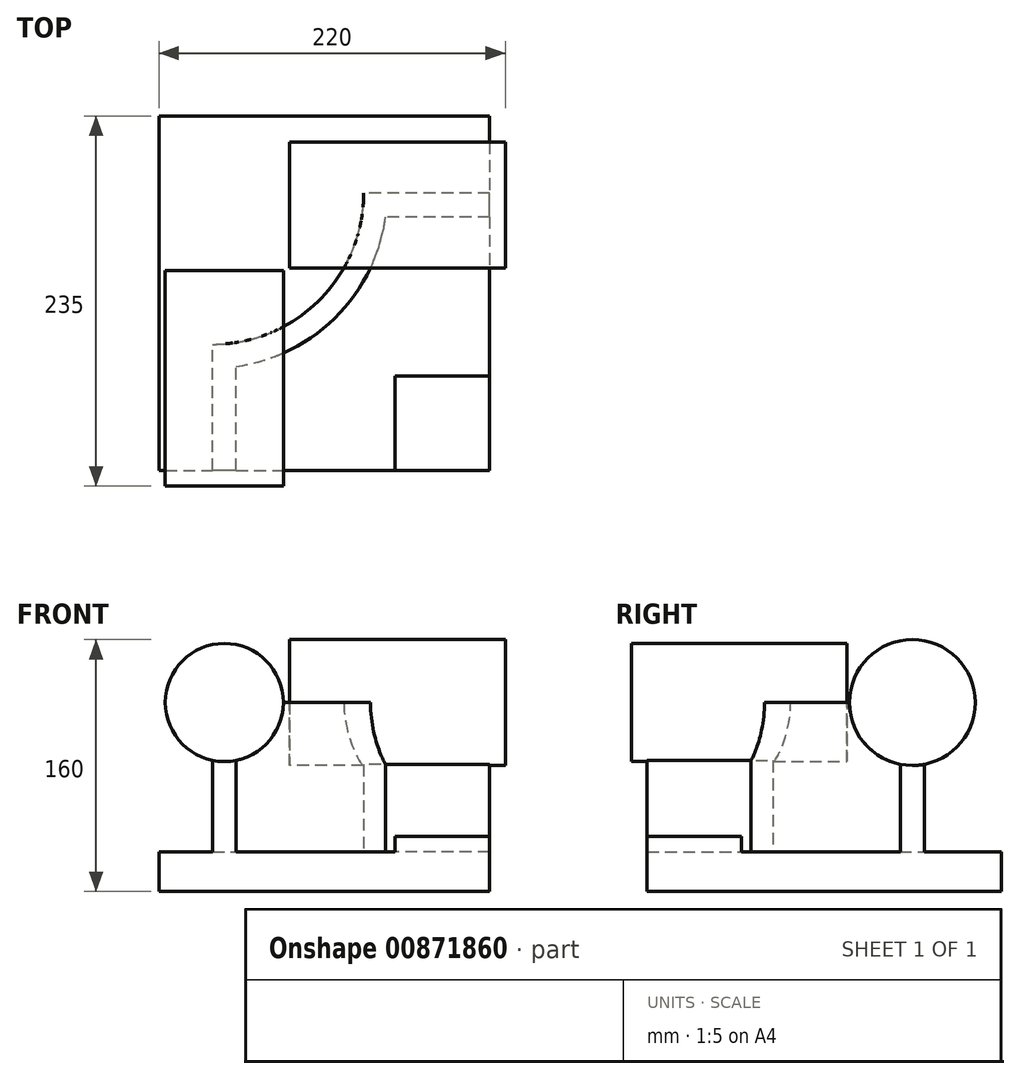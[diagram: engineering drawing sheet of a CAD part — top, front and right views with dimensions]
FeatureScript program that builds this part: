
annotation { "Feature Type Name" : "Feature", "Feature Type Description" : "" }
export const myFeature = defineFeature(function(context is Context, id is Id, definition is map)
    precondition{}
    {
        {
            var Q0;
            Q0=qCreatedBy(makeId("Top.planeOp"),FACE);
            var sketch = newSketch(context, id + "F0", { "sketchPlane" : qUnion([Q0])});
            skLineSegment(sketch, "E0.bottom", {"start": v(-105, 112.5) * mm, "end": v(105, 112.5) * mm});
            skLineSegment(sketch, "E0.top", {"start": v(-105, -112.5) * mm, "end": v(105, -112.5) * mm});
            skLineSegment(sketch, "E0.left", {"start": v(-105, 112.5) * mm, "end": v(-105, -112.5) * mm});
            skLineSegment(sketch, "E0.right", {"start": v(105, 112.5) * mm, "end": v(105, -112.5) * mm});
            skPoint(sketch, "E0.middle", {"position": v(0, 0) * mm});
            skSolve(sketch);
        }
        {
            var Q0;
            Q0=makeQuery(id+"F0.imprint","IMPRINT",FACE,{"disambiguationData":[TD([[makeQuery(id+"F0.imprint","IMPRINT",EDGE,{"derivedFrom":sQuery(id+"F0.wireOp",EDGE,"E0.bottom")}),-1.0]])]});
            extrude(context, id + "F1", {"entities" : qUnion([Q0]), "depth" : 25 * mm, "offsetDistance" : 25 * mm});
        }
        {
            var Q0;
            Q0=makeQuery(id+"F1.opExtrude","CAP_FACE",FACE,{"disambiguationData":[OSD([sQuery(id+"F0.wireOp",EDGE,"E0.bottom"),sQuery(id+"F0.wireOp",EDGE,"E0.top"),sQuery(id+"F0.wireOp",EDGE,"E0.left"),sQuery(id+"F0.wireOp",EDGE,"E0.right")])],"isStart":false});
            var sketch = newSketch(context, id + "F2", { "sketchPlane" : qUnion([Q0])});
            skLineSegment(sketch, "E1", {"start": v(-71, -112.5) * mm, "end": v(-71, -32.5) * mm});
            skLineSegment(sketch, "E2", {"start": v(105, 63.5) * mm, "end": v(25, 63.5) * mm});
            skArc(sketch, "E3", {"start": v(-71, -32.5) * mm, "mid": v(-3.12, -4.38) * mm, "end": v(25, 63.5) * mm});
            skLineSegment(sketch, "E4", {"start": v(-71, 63.5) * mm, "end": v(25, 63.5) * mm, "construction": true});
            skLineSegment(sketch, "E5", {"start": v(-71, 63.5) * mm, "end": v(-71, -32.5) * mm, "construction": true});
            skLineSegment(sketch, "E6.0", {"start": v(-56, -112.5) * mm, "end": v(-56, -46.48) * mm});
            skArc(sketch, "E6.1", {"start": v(-56, -46.48) * mm, "mid": v(7.49, -14.99) * mm, "end": v(38.98, 48.5) * mm});
            skLineSegment(sketch, "E6.2", {"start": v(105, 48.5) * mm, "end": v(38.98, 48.5) * mm});
            skLineSegment(sketch, "E7.0.0", {"start": v(-105, 112.5) * mm, "end": v(-105, -112.5) * mm});
            skLineSegment(sketch, "E7.0.1", {"start": v(-105, -112.5) * mm, "end": v(105, -112.5) * mm});
            skLineSegment(sketch, "E7.0.2", {"start": v(105, -112.5) * mm, "end": v(105, 112.5) * mm});
            skLineSegment(sketch, "E7.0.3", {"start": v(105, 112.5) * mm, "end": v(-105, 112.5) * mm});
            skSolve(sketch);
        }
        {
            var Q0;
            {var subQ2=sQuery(id+"F2.wireOp",EDGE,"E1");Q0=makeQuery(id+"F2.imprint","IMPRINT",FACE,{"disambiguationData":[TD([[makeQuery(id+"F2.imprint","IMPRINT",EDGE,{"derivedFrom":subQ2}),-1.0]])]});}
            extrude(context, id + "F3", {"entities" : qUnion([Q0]), "operationType" : NewBodyOperationType.ADD, "depth" : 95 * mm, "offsetDistance" : 25 * mm});
        }
        {
            var Q0;
            Q0=makeQuery(id+"F3.boolean.opBoolean","MERGE",FACE,{"derivedFrom":[makeQuery(id+"F1.opExtrude","SWEPT_FACE",FACE,{"disambiguationData":[OSD([sQuery(id+"F0.wireOp",EDGE,"E0.top")])]}),makeQuery(id+"F3.opExtrude","SWEPT_FACE",FACE,{"disambiguationData":[OSD([sQuery(id+"F2.wireOp",EDGE,"E7.0.1")])]})]});
            var sketch = newSketch(context, id + "F4", { "sketchPlane" : qUnion([Q0])});
            skCircle(sketch, "E8", {"center": v(-63.5, 120) * mm, "radius": 37.5 * mm});
            skSolve(sketch);
        }
        {
            var Q0;
            Q0 = qSketchRegion(id + "F4", true);
            extrude(context, id + "F5", {"entities" : qUnion([Q0]), "operationType" : NewBodyOperationType.ADD, "depth" : 10 * mm, "offsetDistance" : 25 * mm, "hasSecondDirection" : true, "secondDirectionOppositeDirection" : true, "secondDirectionDepth" : (137 - 10) * mm});
        }
        {
            var Q0;
            Q0=makeQuery(id+"F3.boolean.opBoolean","MERGE",FACE,{"derivedFrom":[makeQuery(id+"F1.opExtrude","SWEPT_FACE",FACE,{"disambiguationData":[OSD([sQuery(id+"F0.wireOp",EDGE,"E0.right")])]}),makeQuery(id+"F3.opExtrude","SWEPT_FACE",FACE,{"disambiguationData":[OSD([sQuery(id+"F2.wireOp",EDGE,"E7.0.2")])]})]});
            var sketch = newSketch(context, id + "F6", { "sketchPlane" : qUnion([Q0])});
            skCircle(sketch, "E9", {"center": v(56, 120) * mm, "radius": 40 * mm});
            skSolve(sketch);
        }
        {
            var Q0;
            Q0 = qSketchRegion(id + "F6", true);
            extrude(context, id + "F7", {"entities" : qUnion([Q0]), "operationType" : NewBodyOperationType.ADD, "depth" : 10 * mm, "offsetDistance" : 25 * mm, "hasSecondDirection" : true, "secondDirectionOppositeDirection" : true, "secondDirectionDepth" : (137 - 10) * mm});
        }
        {
            var Q0;
            {var subQ0=sQuery(id+"F0.wireOp",EDGE,"E0.right");var subQ1=sQuery(id+"F0.wireOp",EDGE,"E0.top");Q0=makeQuery(id+"F3.boolean.opBoolean","SPLIT",FACE,{"disambiguationData":[TD([makeQuery(id+"F3.opExtrude","SWEPT_FACE",FACE,{"disambiguationData":[OSD([sQuery(id+"F2.wireOp",EDGE,"E6.0")])]})])],"derivedFrom":makeQuery(id+"F1.opExtrude","CAP_FACE",FACE,{"disambiguationData":[OSD([sQuery(id+"F0.wireOp",EDGE,"E0.bottom"),subQ1,sQuery(id+"F0.wireOp",EDGE,"E0.left"),subQ0])],"isStart":false})});}
            var sketch = newSketch(context, id + "F8", { "sketchPlane" : qUnion([Q0])});
            skLineSegment(sketch, "E10.bottom", {"start": v(105, -112.5) * mm, "end": v(45, -112.5) * mm});
            skLineSegment(sketch, "E10.top", {"start": v(105, -52.5) * mm, "end": v(45, -52.5) * mm});
            skLineSegment(sketch, "E10.left", {"start": v(105, -112.5) * mm, "end": v(105, -52.5) * mm});
            skLineSegment(sketch, "E10.right", {"start": v(45, -112.5) * mm, "end": v(45, -52.5) * mm});
            skSolve(sketch);
        }
        {
            var Q0;
            Q0 = qSketchRegion(id + "F8", true);
            extrude(context, id + "F9", {"entities" : qUnion([Q0]), "operationType" : NewBodyOperationType.ADD, "depth" : (35 - 25) * mm, "offsetDistance" : 25 * mm});
        }
    });
